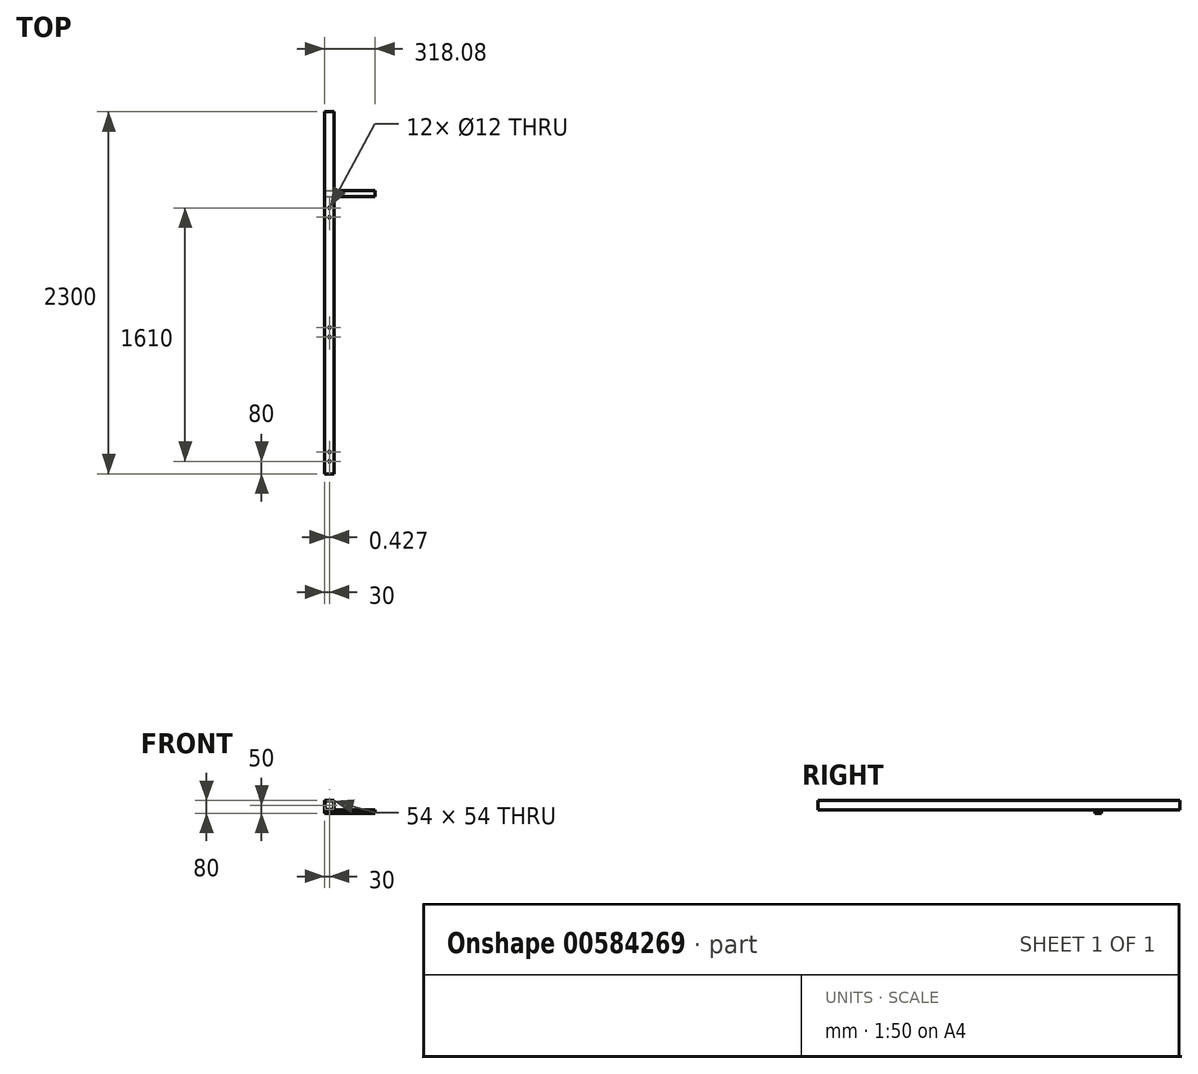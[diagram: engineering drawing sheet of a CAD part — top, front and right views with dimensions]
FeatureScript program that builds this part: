
annotation { "Feature Type Name" : "Feature", "Feature Type Description" : "" }
export const myFeature = defineFeature(function(context is Context, id is Id, definition is map)
    precondition{}
    {
        {
            var Q0;
            Q0=qCreatedBy(makeId("Front.planeOp"),FACE);
            var sketch = newSketch(context, id + "F0", { "sketchPlane" : qUnion([Q0])});
            skLineSegment(sketch, "E0.bottom", {"start": v(0, 0) * mm, "end": v(60, 0) * mm});
            skLineSegment(sketch, "E0.top", {"start": v(0, -60) * mm, "end": v(60, -60) * mm});
            skLineSegment(sketch, "E0.left", {"start": v(0, 0) * mm, "end": v(0, -60) * mm});
            skLineSegment(sketch, "E0.right", {"start": v(60, 0) * mm, "end": v(60, -60) * mm});
            skLineSegment(sketch, "E1.bottom", {"start": v(3, -3) * mm, "end": v(57, -3) * mm});
            skLineSegment(sketch, "E1.top", {"start": v(3, -57) * mm, "end": v(57, -57) * mm});
            skLineSegment(sketch, "E1.left", {"start": v(3, -3) * mm, "end": v(3, -57) * mm});
            skLineSegment(sketch, "E1.right", {"start": v(57, -3) * mm, "end": v(57, -57) * mm});
            skSolve(sketch);
        }
        {
            var Q0;
            Q0=makeQuery(id+"F0.imprint","IMPRINT",FACE,{"disambiguationData":[TD([[makeQuery(id+"F0.imprint","IMPRINT",EDGE,{"derivedFrom":sQuery(id+"F0.wireOp",EDGE,"E0.bottom")}),-1.0]])]});
            extrude(context, id + "F1", {"entities" : qUnion([Q0]), "depth" : 2300 * mm, "offsetDistance" : 25 * mm});
        }
        {
            var Q0;
            Q0=makeQuery(id+"F1.opExtrude","SWEPT_FACE",FACE,{"disambiguationData":[OSD([sQuery(id+"F0.wireOp",EDGE,"E0.top")])]});
            var sketch = newSketch(context, id + "F2", { "sketchPlane" : qUnion([Q0])});
            skCircle(sketch, "E2", {"center": v(30, 2220) * mm, "radius": 6 * mm});
            skCircle(sketch, "E3", {"center": v(30, 2160) * mm, "radius": 6 * mm});
            skCircle(sketch, "E4", {"center": v(30, 1430) * mm, "radius": 6 * mm});
            skCircle(sketch, "E5", {"center": v(30.43, 1370) * mm, "radius": 6 * mm});
            skCircle(sketch, "E6", {"center": v(30, 670) * mm, "radius": 6 * mm});
            skCircle(sketch, "E7", {"center": v(30, 610) * mm, "radius": 6 * mm});
            skSolve(sketch);
        }
        {
            var Q0;
            Q0=makeQuery(id+"F2.imprint","IMPRINT",FACE,{"disambiguationData":[TD([[makeQuery(id+"F2.imprint","IMPRINT",EDGE,{"derivedFrom":sQuery(id+"F2.wireOp",EDGE,"E7")}),1.0]])]});
            var Q1;
            Q1=makeQuery(id+"F2.imprint","IMPRINT",FACE,{"disambiguationData":[TD([[makeQuery(id+"F2.imprint","IMPRINT",EDGE,{"derivedFrom":sQuery(id+"F2.wireOp",EDGE,"E6")}),1.0]])]});
            var Q2;
            Q2=makeQuery(id+"F2.imprint","IMPRINT",FACE,{"disambiguationData":[TD([[makeQuery(id+"F2.imprint","IMPRINT",EDGE,{"derivedFrom":sQuery(id+"F2.wireOp",EDGE,"E4")}),1.0]])]});
            var Q3;
            Q3=makeQuery(id+"F2.imprint","IMPRINT",FACE,{"disambiguationData":[TD([[makeQuery(id+"F2.imprint","IMPRINT",EDGE,{"derivedFrom":sQuery(id+"F2.wireOp",EDGE,"E5")}),1.0]])]});
            var Q4;
            Q4=makeQuery(id+"F2.imprint","IMPRINT",FACE,{"disambiguationData":[TD([[makeQuery(id+"F2.imprint","IMPRINT",EDGE,{"derivedFrom":sQuery(id+"F2.wireOp",EDGE,"E2")}),1.0]])]});
            var Q5;
            Q5=makeQuery(id+"F2.imprint","IMPRINT",FACE,{"disambiguationData":[TD([[makeQuery(id+"F2.imprint","IMPRINT",EDGE,{"derivedFrom":sQuery(id+"F2.wireOp",EDGE,"E3")}),1.0]])]});
            var Q6;
            Q6=sQuery(id+"F2.wireOp",EDGE,"E5");
            var Q7;
            Q7=sQuery(id+"F2.wireOp",EDGE,"E4");
            var Q8;
            Q8=sQuery(id+"F2.wireOp",EDGE,"E2");
            var Q9;
            Q9=sQuery(id+"F2.wireOp",EDGE,"E3");
            var Q10;
            Q10=sQuery(id+"F2.wireOp",EDGE,"E6");
            var Q11;
            Q11=sQuery(id+"F2.wireOp",EDGE,"E7");
            extrude(context, id + "F3", {"entities" : qUnion([Q0, Q1, Q2, Q3, Q4, Q5]), "operationType" : NewBodyOperationType.REMOVE, "surfaceEntities" : qUnion([Q6, Q7, Q8, Q9, Q10, Q11]), "oppositeDirection" : true, "depth" : 100 * mm, "offsetDistance" : 25 * mm});
        }
        {
            var Q0;
            Q0=makeQuery(id+"F1.opExtrude","SWEPT_FACE",FACE,{"disambiguationData":[OSD([sQuery(id+"F0.wireOp",EDGE,"E0.top")])]});
            var sketch = newSketch(context, id + "F4", { "sketchPlane" : qUnion([Q0])});
            skLineSegment(sketch, "E8.bottom", {"start": v(0, 540) * mm, "end": v(318.08, 540) * mm});
            skLineSegment(sketch, "E8.top", {"start": v(0, 500) * mm, "end": v(318.08, 500) * mm});
            skLineSegment(sketch, "E8.left", {"start": v(0, 540) * mm, "end": v(0, 500) * mm});
            skLineSegment(sketch, "E8.right", {"start": v(318.08, 540) * mm, "end": v(318.08, 500) * mm});
            skSolve(sketch);
        }
        {
            var Q0;
            Q0 = qSketchRegion(id + "F4", true);
            extrude(context, id + "F5", {"entities" : qUnion([Q0]), "operationType" : NewBodyOperationType.ADD, "depth" : 20 * mm, "offsetDistance" : 25 * mm});
        }
    });
